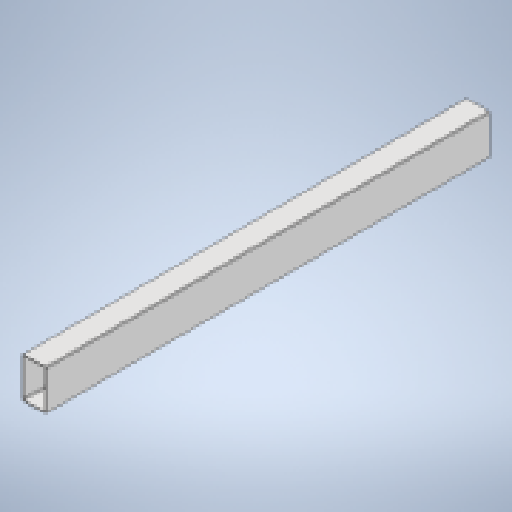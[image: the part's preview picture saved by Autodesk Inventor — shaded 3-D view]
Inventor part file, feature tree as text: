
AUTODESK INVENTOR PART (.ipt)
format: ipt  version: 2023 (Build 270158000, 158)  size: 180,736 bytes
history: native  units: in
note: dims shown in document units (in); Inventor stores cm internally (conversion verified against a paired STEP export)
features: extrude x2, sketch x2, shell x1, fillet x1
ambient origin geometry x8: Origin, YZ Plane, XZ Plane, XY Plane, X Axis, Y Axis, Z Axis, Center Point
bodies: Solid1 (feature_tree)
feature tree (6):
  extrude  "Extrusion1"  Depth=5.0in
  shell  "Shell1"  Thickness=55.0in
  fillet  "Fillet1"  Radius=0.125in
  extrude  "Extrusion2"  Depth=3.0in
  sketch  "Sketch1"  dims[d0=3.0in d1=5.0in d2=55.0in d3=0.0in d4=0.125in]
  sketch  "Sketch2"  dims[d5=0.125in d6=3.0in d7=3.0in d8=2.0866in d9=1.5748in d10=0.315in d11=0.7874in d13=52.0in d14=0.3937in d16=1.0in d18=49.0in d19=0.0in]
